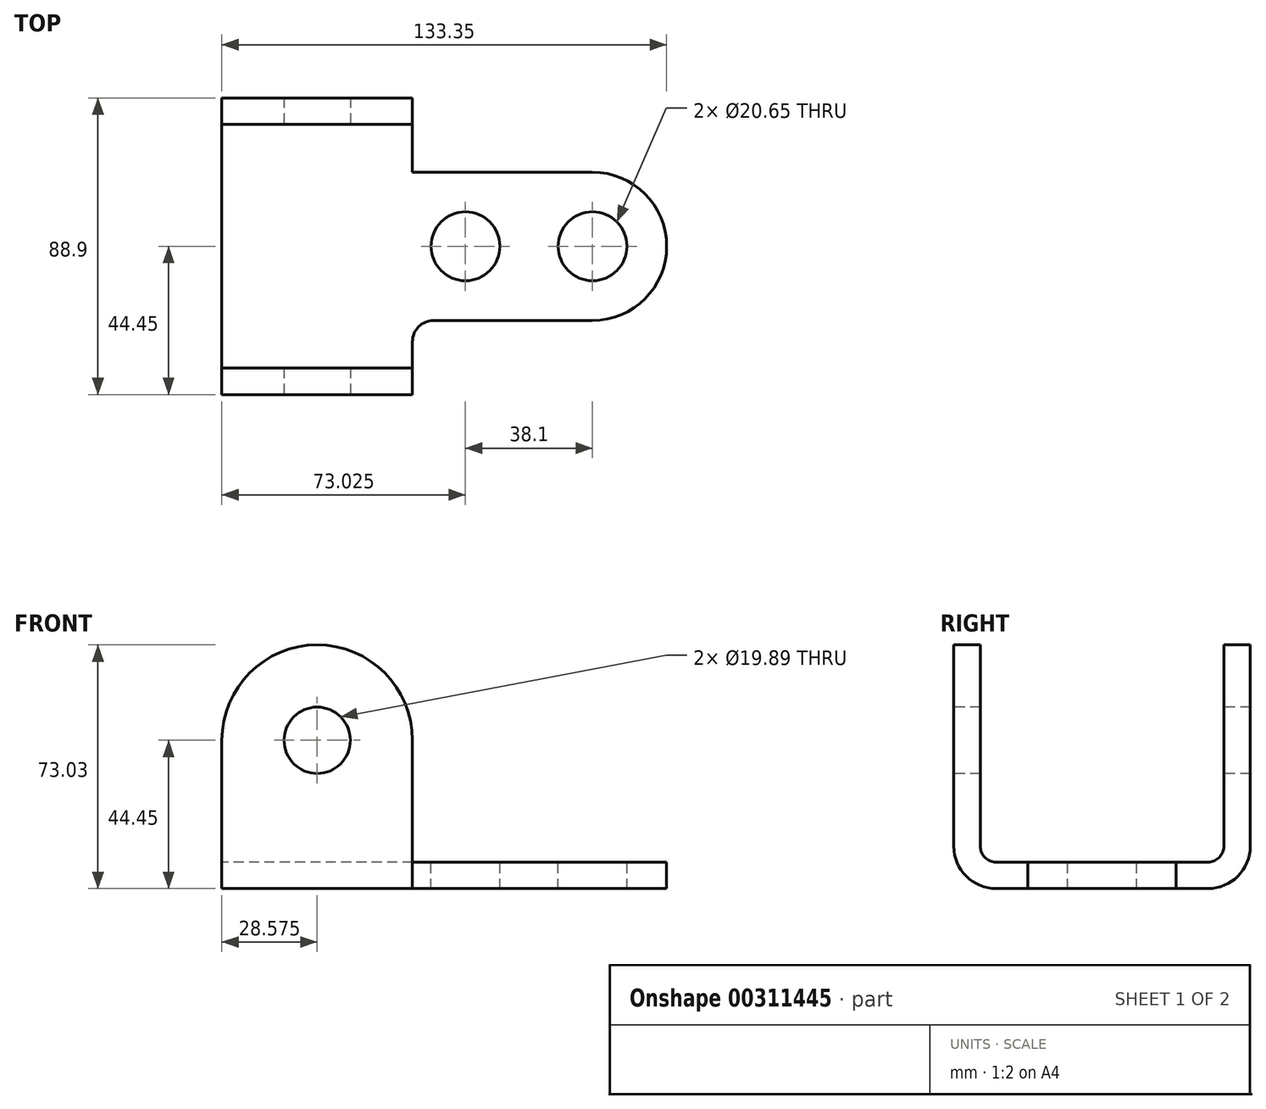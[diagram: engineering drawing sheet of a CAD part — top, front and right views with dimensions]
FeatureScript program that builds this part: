
annotation { "Feature Type Name" : "Feature", "Feature Type Description" : "" }
export const myFeature = defineFeature(function(context is Context, id is Id, definition is map)
    precondition{}
    {
        {
            var Q0;
            Q0=qCreatedBy(makeId("Right.planeOp"),FACE);
            var sketch = newSketch(context, id + "F0", { "sketchPlane" : qUnion([Q0])});
            skLineSegment(sketch, "E0", {"start": v(12.7, 0) * mm, "end": v(76.2, 0) * mm});
            skLineSegment(sketch, "E1", {"start": v(88.9, 12.7) * mm, "end": v(88.9, 73.03) * mm});
            skLineSegment(sketch, "E2", {"start": v(88.9, 73.03) * mm, "end": v(80.96, 73.03) * mm});
            skLineSegment(sketch, "E3", {"start": v(0, 12.7) * mm, "end": v(0, 73.03) * mm});
            skLineSegment(sketch, "E4", {"start": v(0, 73.03) * mm, "end": v(7.94, 73.03) * mm});
            skLineSegment(sketch, "E5", {"start": v(7.94, 73.03) * mm, "end": v(7.94, 12.7) * mm});
            skLineSegment(sketch, "E6", {"start": v(12.7, 7.94) * mm, "end": v(76.2, 7.94) * mm});
            skLineSegment(sketch, "E7", {"start": v(80.96, 12.7) * mm, "end": v(80.96, 73.03) * mm});
            skPoint(sketch, "E8.visualSharp", {"position": v(0, 0) * mm});
            skArc(sketch, "E8.filletArc", {"start": v(0, 12.7) * mm, "mid": v(3.72, 3.72) * mm, "end": v(12.7, 0) * mm});
            skPoint(sketch, "E9.visualSharp", {"position": v(88.9, 0) * mm});
            skArc(sketch, "E9.filletArc", {"start": v(76.2, 0) * mm, "mid": v(85.18, 3.72) * mm, "end": v(88.9, 12.7) * mm});
            skPoint(sketch, "E10.visualSharp", {"position": v(80.96, 7.94) * mm});
            skArc(sketch, "E10.filletArc", {"start": v(76.2, 7.94) * mm, "mid": v(79.57, 9.33) * mm, "end": v(80.96, 12.7) * mm});
            skPoint(sketch, "E11.visualSharp", {"position": v(7.94, 7.94) * mm});
            skArc(sketch, "E11.filletArc", {"start": v(7.94, 12.7) * mm, "mid": v(9.33, 9.33) * mm, "end": v(12.7, 7.94) * mm});
            skSolve(sketch);
        }
        {
            var Q0;
            Q0 = qSketchRegion(id + "F0", true);
            extrude(context, id + "F1", {"entities" : qUnion([Q0]), "depth" : 57.15 * mm});
        }
        {
            var Q0;
            Q0=makeQuery(id+"F1.opExtrude","SWEPT_FACE",FACE,{"disambiguationData":[OSD([sQuery(id+"F0.wireOp",EDGE,"E3")])]});
            var sketch = newSketch(context, id + "F2", { "sketchPlane" : qUnion([Q0])});
            skCircle(sketch, "E12", {"center": v(28.58, 44.45) * mm, "radius": 9.95 * mm});
            skPoint(sketch, "E12.centerSnap0", {"position": v(28.58, 73.03) * mm});
            skSolve(sketch);
        }
        {
            var Q0;
            Q0 = qSketchRegion(id + "F2", true);
            extrude(context, id + "F3", {"entities" : qUnion([Q0]), "operationType" : NewBodyOperationType.REMOVE, "oppositeDirection" : true, "depth" : 88.9 * mm});
        }
        {
            var Q0;
            Q0=makeQuery(id+"F1.opExtrude","SWEPT_FACE",FACE,{"disambiguationData":[OSD([sQuery(id+"F0.wireOp",EDGE,"E3")])]});
            var sketch = newSketch(context, id + "F4", { "sketchPlane" : qUnion([Q0])});
            skCircle(sketch, "E13", {"center": v(28.58, 44.45) * mm, "radius": 28.58 * mm});
            skLineSegment(sketch, "E14", {"start": v(0, 73.03) * mm, "end": v(57.15, 73.03) * mm});
            skLineSegment(sketch, "E15", {"start": v(57.15, 73.03) * mm, "end": v(57.15, 42.86) * mm});
            skLineSegment(sketch, "E16", {"start": v(0, 73.03) * mm, "end": v(0, 42.86) * mm});
            skSolve(sketch);
        }
        {
            var Q0;
            {var subQ0=sQuery(id+"F4.wireOp",EDGE,"E14");var subQ1=sQuery(id+"F4.wireOp",EDGE,"E13");var subQ2=makeQuery(id+"F4.imprint","INTERSECT",VERTEX,{"derivedFrom":[subQ1,subQ0]});Q0=makeQuery(id+"F4.imprint","IMPRINT",FACE,{"disambiguationData":[TD([[makeQuery(id+"F4.imprint","IMPRINT",EDGE,{"disambiguationData":[TD([[subQ2,-1.0]])],"derivedFrom":subQ1}),-1.0]])]});}
            var Q1;
            {var subQ0=sQuery(id+"F4.wireOp",EDGE,"E14");var subQ1=sQuery(id+"F4.wireOp",EDGE,"E13");var subQ2=makeQuery(id+"F4.imprint","INTERSECT",VERTEX,{"derivedFrom":[subQ1,subQ0]});Q1=makeQuery(id+"F4.imprint","IMPRINT",FACE,{"disambiguationData":[TD([[makeQuery(id+"F4.imprint","IMPRINT",EDGE,{"disambiguationData":[TD([[subQ2,1.0]])],"derivedFrom":subQ1}),-1.0]])]});}
            extrude(context, id + "F5", {"entities" : qUnion([Q0, Q1]), "operationType" : NewBodyOperationType.REMOVE, "oppositeDirection" : true, "depth" : 88.9 * mm});
        }
        {
            var Q0;
            Q0=makeQuery(id+"F1.opExtrude","SWEPT_FACE",FACE,{"disambiguationData":[OSD([sQuery(id+"F0.wireOp",EDGE,"E6")])]});
            var sketch = newSketch(context, id + "F6", { "sketchPlane" : qUnion([Q0])});
            skPoint(sketch, "E17.start.orphan", {"position": v(57.15, 44.45) * mm});
            skLineSegment(sketch, "E18", {"start": v(57.15, 66.67) * mm, "end": v(57.15, 22.23) * mm});
            skLineSegment(sketch, "E19", {"start": v(57.15, 66.67) * mm, "end": v(133.35, 66.67) * mm});
            skLineSegment(sketch, "E20", {"start": v(133.35, 66.67) * mm, "end": v(133.35, 22.23) * mm});
            skLineSegment(sketch, "E21", {"start": v(133.35, 22.23) * mm, "end": v(57.15, 22.23) * mm});
            skSolve(sketch);
        }
        {
            var Q0;
            Q0 = qSketchRegion(id + "F6", true);
            extrude(context, id + "F7", {"entities" : qUnion([Q0]), "operationType" : NewBodyOperationType.ADD, "oppositeDirection" : true, "depth" : 7.94 * mm});
        }
        {
            var Q0;
            Q0=makeQuery(id+"F7.boolean.opBoolean","MERGE",FACE,{"derivedFrom":[makeQuery(id+"F1.opExtrude","SWEPT_FACE",FACE,{"disambiguationData":[OSD([sQuery(id+"F0.wireOp",EDGE,"E6")])]}),makeQuery(id+"F7.opExtrude","CAP_FACE",FACE,{"disambiguationData":[OSD([sQuery(id+"F6.wireOp",EDGE,"E18"),sQuery(id+"F6.wireOp",EDGE,"E19"),sQuery(id+"F6.wireOp",EDGE,"E20"),sQuery(id+"F6.wireOp",EDGE,"E21")])],"isStart":true})]});
            var sketch = newSketch(context, id + "F8", { "sketchPlane" : qUnion([Q0])});
            skCircle(sketch, "E22", {"center": v(73.03, 44.45) * mm, "radius": 10.33 * mm});
            skPoint(sketch, "E22.centerSnap0", {"position": v(133.35, 44.45) * mm});
            skCircle(sketch, "E23", {"center": v(111.12, 44.45) * mm, "radius": 10.33 * mm});
            skCircle(sketch, "E24", {"center": v(111.12, 44.45) * mm, "radius": 22.23 * mm});
            skLineSegment(sketch, "E25", {"start": v(133.35, 44.45) * mm, "end": v(133.35, 66.67) * mm});
            skLineSegment(sketch, "E26", {"start": v(133.35, 66.67) * mm, "end": v(111.12, 66.67) * mm});
            skLineSegment(sketch, "E27", {"start": v(133.35, 44.45) * mm, "end": v(133.35, 22.23) * mm});
            skLineSegment(sketch, "E28", {"start": v(133.35, 22.23) * mm, "end": v(111.12, 22.22) * mm});
            skSolve(sketch);
        }
        {
            var Q0;
            Q0=makeQuery(id+"F8.imprint","IMPRINT",FACE,{"disambiguationData":[TD([[makeQuery(id+"F8.imprint","IMPRINT",EDGE,{"derivedFrom":sQuery(id+"F8.wireOp",EDGE,"E22")}),1.0]])]});
            var Q1;
            Q1=makeQuery(id+"F8.imprint","IMPRINT",FACE,{"disambiguationData":[TD([[makeQuery(id+"F8.imprint","IMPRINT",EDGE,{"derivedFrom":sQuery(id+"F8.wireOp",EDGE,"E23")}),1.0]])]});
            var Q2;
            {var subQ0=sQuery(id+"F8.wireOp",EDGE,"E25");Q2=makeQuery(id+"F8.imprint","IMPRINT",FACE,{"disambiguationData":[TD([[makeQuery(id+"F8.imprint","IMPRINT",EDGE,{"derivedFrom":subQ0}),-1.0]])]});}
            var Q3;
            {var subQ0=sQuery(id+"F8.wireOp",EDGE,"E27");Q3=makeQuery(id+"F8.imprint","IMPRINT",FACE,{"disambiguationData":[TD([[makeQuery(id+"F8.imprint","IMPRINT",EDGE,{"derivedFrom":subQ0}),-1.0]])]});}
            extrude(context, id + "F9", {"entities" : qUnion([Q0, Q1, Q2, Q3]), "operationType" : NewBodyOperationType.REMOVE, "oppositeDirection" : true, "depth" : 25.4 * mm});
        }
        {
            var Q0;
            Q0=makeQuery(id+"F7.opExtrude","SWEPT_EDGE",EDGE,{"disambiguationData":[OSD([sQuery(id+"F0.wireOp",EDGE,"E6"),sQuery(id+"F6.wireOp",EDGE,"E18"),sQuery(id+"F6.wireOp",EDGE,"E21")])]});
            var Q1;
            Q1=makeQuery(id+"F7.opExtrude","SWEPT_EDGE",EDGE,{"disambiguationData":[OSD([sQuery(id+"F0.wireOp",EDGE,"E6"),sQuery(id+"F6.wireOp",EDGE,"E18"),sQuery(id+"F6.wireOp",EDGE,"E19")])]});
            fillet(context, id + "F10", {"entities" : qUnion([Q0, Q1]), "radius" : 6.35 * mm, "tangentPropagation" : true, "allowEdgeOverflow" : false});
        }
    });
